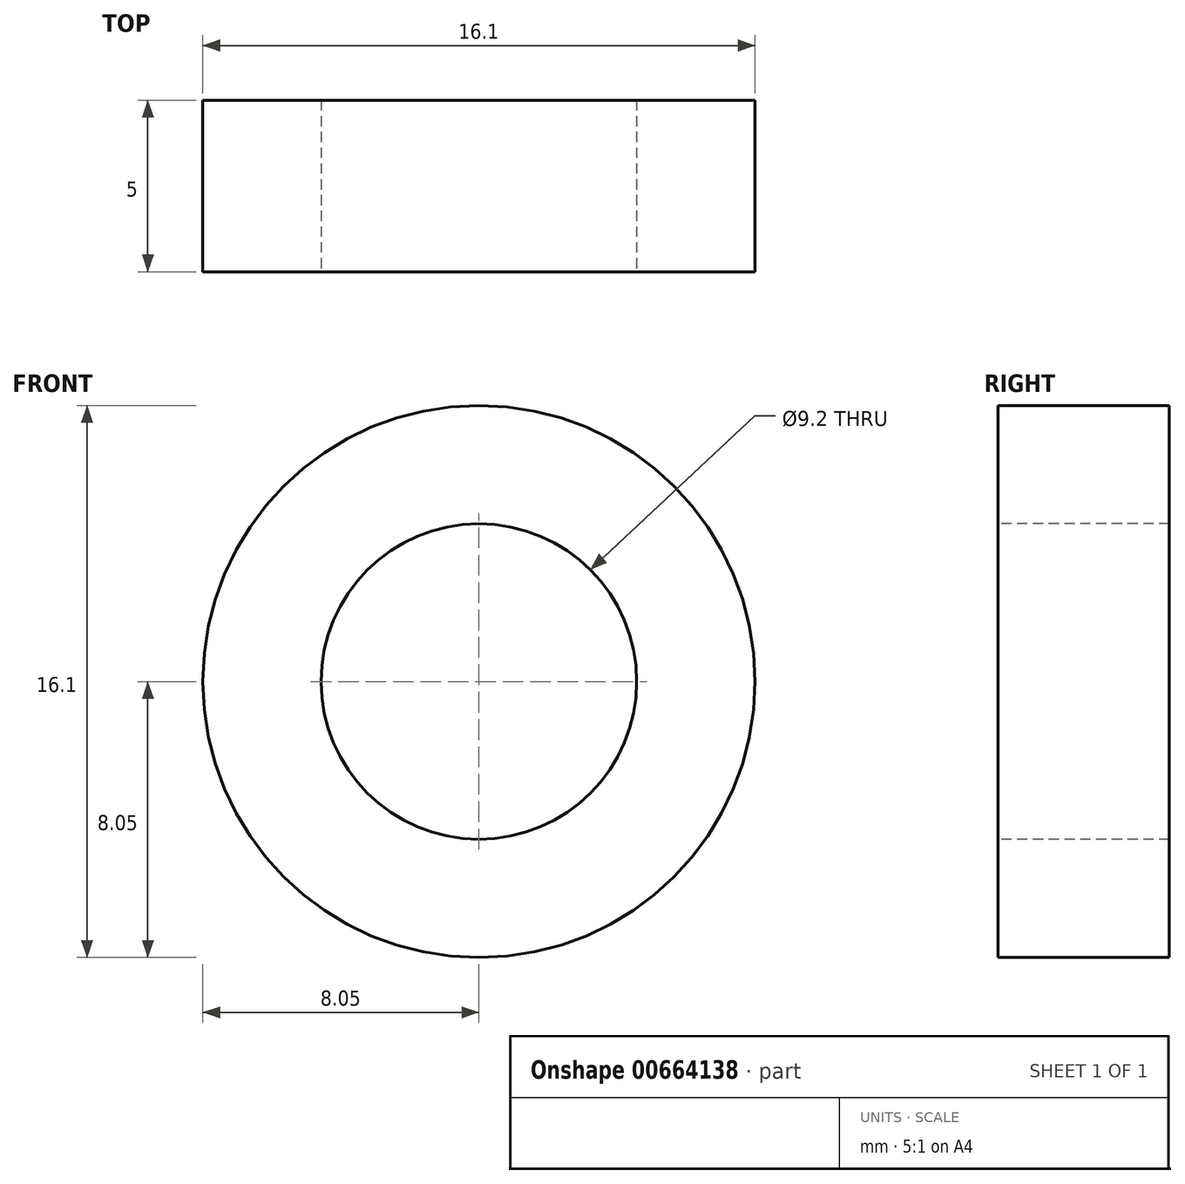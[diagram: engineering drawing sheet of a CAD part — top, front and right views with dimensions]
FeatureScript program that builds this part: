
annotation { "Feature Type Name" : "Feature", "Feature Type Description" : "" }
export const myFeature = defineFeature(function(context is Context, id is Id, definition is map)
    precondition{}
    {
        {
            var Q0;
            Q0=qCreatedBy(makeId("Front.planeOp"),FACE);
            var sketch = newSketch(context, id + "F0", { "sketchPlane" : qUnion([Q0])});
            skCircle(sketch, "E0", {"center": v(0, 0) * mm, "radius": 8.05 * mm});
            skSolve(sketch);
        }
        {
            var Q0;
            Q0=qSketchRegion(id+"F0",true);
            extrude(context, id + "F1", {"entities" : qUnion([Q0]), "depth" : 5 * mm, "offsetDistance" : 25 * mm});
        }
        {
            var Q0;
            Q0=makeQuery(id+"F1.opExtrude","CAP_FACE",FACE,{"disambiguationData":[OSD([sQuery(id+"F0.wireOp",EDGE,"E0")])],"isStart":false});
            var sketch = newSketch(context, id + "F2", { "sketchPlane" : qUnion([Q0])});
            skCircle(sketch, "E1", {"center": v(0, 0) * mm, "radius": 4.55 * mm});
            skSolve(sketch);
        }
        {
            var Q0;
            Q0=sQuery(id+"F2.wireOp",VERTEX,"E1.center");
            var Q1;
            Q1=makeQuery(id+"F1.opExtrude","SWEPT_BODY",BODY,{"disambiguationData":[OSD([sQuery(id+"F0.wireOp",EDGE,"E0")])]});
            hole(context, id + "F3", {"style" : HoleStyle.SIMPLE, "endStyle" : HoleEndStyle.THROUGH, "holeDiameter" : 9.2 * mm, "majorDiameter" : 5 * mm, "isTappedThrough" : true, "tappedDepth" : 12 * mm, "tapClearance" : 3, "locations" : qUnion([Q0]), "scope" : qUnion([Q1])});
        }
    });
